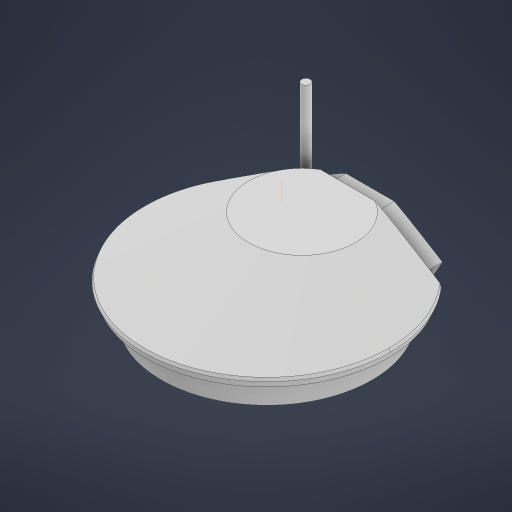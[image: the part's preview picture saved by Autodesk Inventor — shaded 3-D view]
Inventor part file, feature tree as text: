
AUTODESK INVENTOR PART (.ipt)
format: ipt  version: 2024 (Build 280153000, 153)  size: 315,392 bytes
history: native  units: in
note: dims shown in document units (in); Inventor stores cm internally (conversion verified against a paired STEP export)
features: sketch x9, extrude x3, projected_geometry x3, other x2, plane x2, chamfer x2, revolve x1, loft x1
ambient origin geometry x8: Origin, YZ Plane, XZ Plane, XY Plane, X Axis, Y Axis, Z Axis, Center Point
bodies: Solid1 (feature_tree)
feature tree (23):
  sketch  "Sketch1"  dims[d0=1.75in d1=0.1512in]
  sketch  "Sketch2"  dims[d2=7.0in d3=0.5118in]
  revolve  "Revolution1"  [1 undecoded]
  sketch  "Sketch3"  dims[d5=0.2756in]
  other  "Work Axis1"
  sketch  "Sketch4"  dims[d6=2.5in]
  plane  "Work Plane1"
  sketch  "Sketch5"  dims[d7=6.0in]
  plane  "Work Plane2"
  loft  "Loft1"
  chamfer  "Chamfer1"  Distance=2.75in
  extrude  "Extrusion2"  TaperAngle=360.0deg  [1 undecoded]
  extrude  "Extrusion3"  Depth=7.4in
  extrude  "Extrusion4"  Depth=7.0in
  chamfer  "Chamfer2"  Angle=90.0deg  [1 undecoded]
  projected_geometry  "Projected Loop1"
  projected_geometry  "Projected Loop2"
  sketch  "Sketch6"  dims[d8=6.0in]
  other  "Edges1"
  sketch  "Sketch7"  dims[d9=6.0in]
  sketch  "Sketch8"  dims[d10=6.0in]
  projected_geometry  "Projected Loop3"
  sketch  "Sketch9"  dims[d11=1.2in d12=2.75in d13=360.0deg d14=7.4in d15=7.0in d16=90.0deg d20=2.25in d21=6.0in d22=0.0in d23=90.0deg d24=0.0in d25=90.0deg d26=0.125in d27=0.125in d28=45.0deg d29=8.875in d30=0.0in d31=1.25in d32=0.0in d33=7.0in d34=0.0in d35=0.25in d36=0.125in d37=45.0deg d38=6.5327in]
note: 3 required parameter values undecoded (feature->parameter linkage not recoverable at this tier; creation-order binding heuristic only, values carry confidence <= 0.55)